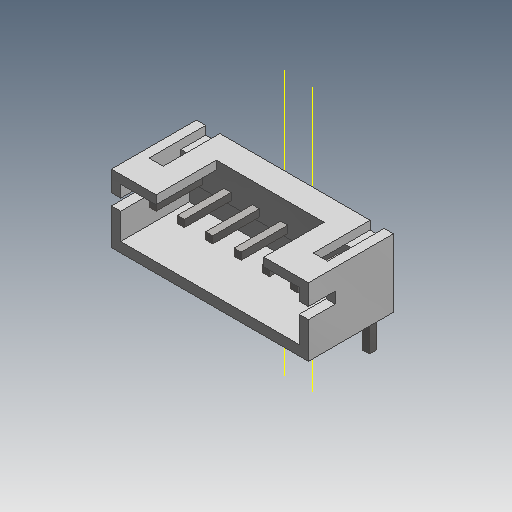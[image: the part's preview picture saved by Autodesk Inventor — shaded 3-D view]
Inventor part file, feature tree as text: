
AUTODESK INVENTOR PART (.ipt)
format: ipt  version: 2020.2 (Build 242310000, 310)  size: 365,056 bytes
history: native  units: mm (DEFAULTED — no unit token found)
features: sketch x13, projected_geometry x12, extrude x8, plane x7, other x3, surface_op x2, split x1
ambient origin geometry x8: Origin, YZ Plane, XZ Plane, XY Plane, X Axis, Y Axis, Z Axis, Center Point
bodies: Solid3 (feature_tree), Solid4 (feature_tree), Solid5 (feature_tree)
feature tree (46):
  surface_op  "Sculpt1"
  plane  "Work Plane2"
  split  "Split1"
  plane  "Work Plane1"
  extrude  "Extrusion6"  Depth=0.8mm
  extrude  "Extrusion5"  Depth=1.0mm
  extrude  "Extrusion4"  Depth=0.8mm
  extrude  "Extrusion3"  Depth=3.3mm
  extrude  "Extrusion2"  Depth=3.3mm
  extrude  "Extrusion1"  Depth=3.3mm
  extrude  "Extrusion17"  Depth=0.95mm
  extrude  "Extrusion18"  [1 undecoded]
  plane  "Work Plane3"
  plane  "Work Plane4"
  plane  "Work Plane5"
  plane  "Work Plane6"
  plane  "Work Plane7"
  other  "Work Axis1"
  other  "Work Axis2"
  sketch  "Sketch1"  dims[d0=-2.65mm d1=0.8mm d2=0.0mm]
  sketch  "Sketch2"  dims[d3=1.0mm d4=-0.0mm d5=1.0mm d6=-0.0mm]
  sketch  "Sketch3"  dims[d7=3.4mm d8=0.0mm d9=0.8mm d10=-0.0mm]
  sketch  "Sketch4"  dims[d11=3.3mm d12=-0.0mm d13=3.3mm d14=0.0mm]
  sketch  "Sketch5"  dims[d15=3.3mm d16=0.0mm d17=3.3mm d18=-0.0mm]
  sketch  "Sketch6"  dims[d19=3.3mm d20=-0.0mm d21=3.3mm d22=0.0mm]
  sketch  "Sketch7"  dims[d23=0.0mm d24=0.95mm d25=0.0mm]
  sketch  "Sketch8"  dims[d26=3.3mm d27=0.0mm]
  sketch  "Sketch9"
  sketch  "Sketch10"
  sketch  "Sketch11"
  sketch  "Sketch12"
  projected_geometry  "Projected Loop1"
  projected_geometry  "Projected Loop2"
  projected_geometry  "Projected Loop3"
  projected_geometry  "Projected Loop4"
  projected_geometry  "Projected Loop5"
  projected_geometry  "Projected Loop6"
  sketch  "Sketch13"
  projected_geometry  "Projected Loop7"
  projected_geometry  "Projected Loop8"
  projected_geometry  "Projected Loop9"
  projected_geometry  "Projected Loop10"
  projected_geometry  "Projected Loop11"
  projected_geometry  "Projected Loop12"
  surface_op  "Surface1"
  other  "Srf1"
note: 1 required parameter value undecoded (feature->parameter linkage not recoverable at this tier; creation-order binding heuristic only, values carry confidence <= 0.55)
